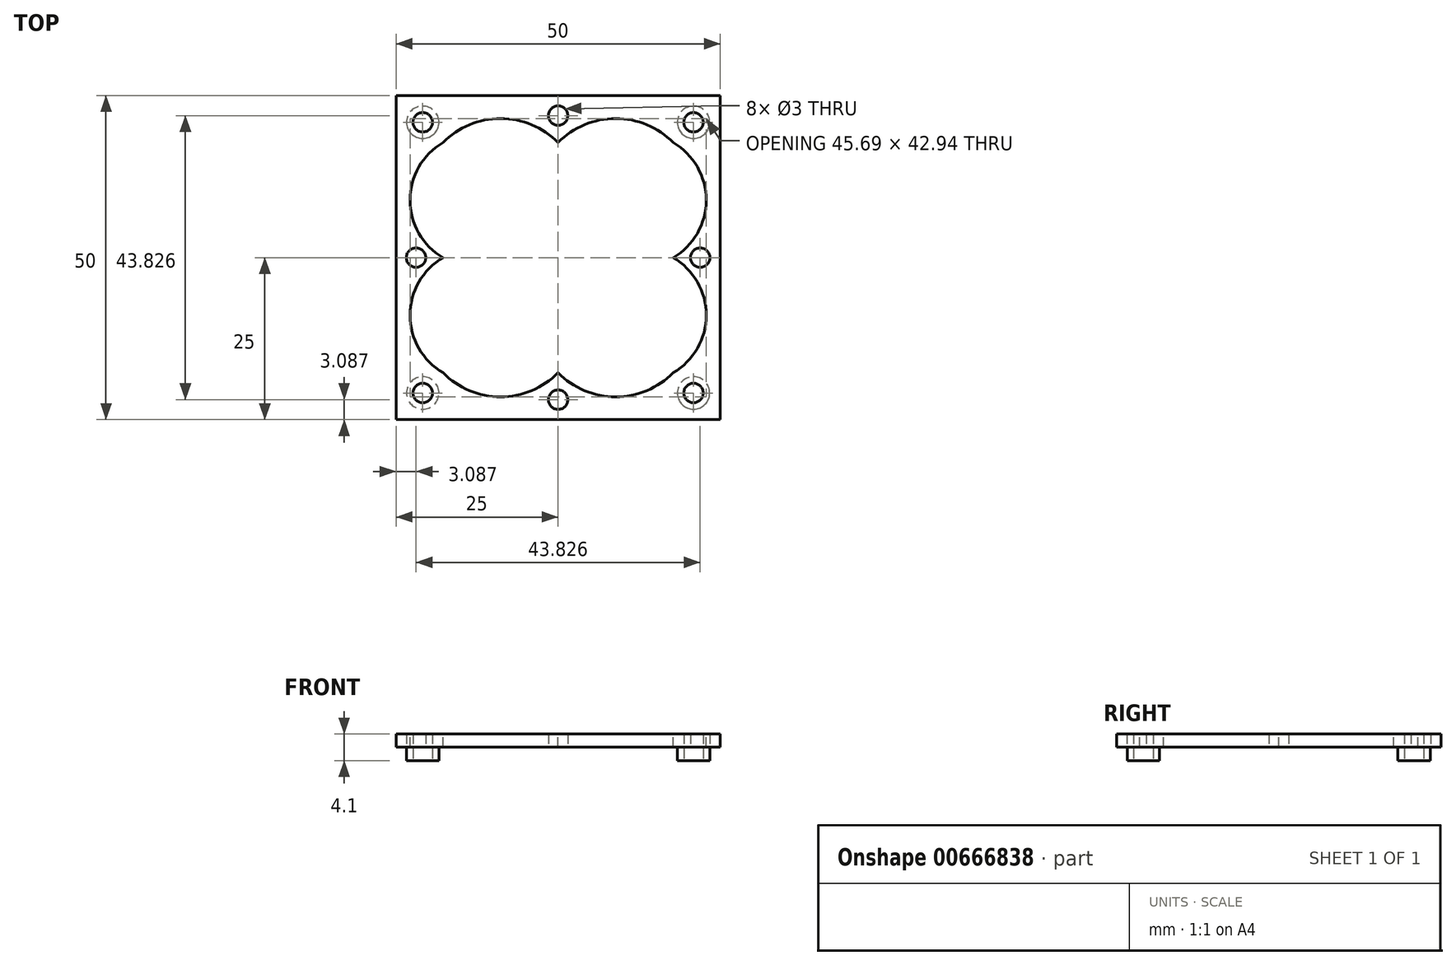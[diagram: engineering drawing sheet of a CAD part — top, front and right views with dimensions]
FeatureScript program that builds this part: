
annotation { "Feature Type Name" : "Feature", "Feature Type Description" : "" }
export const myFeature = defineFeature(function(context is Context, id is Id, definition is map)
    precondition{}
    {
        {
            var Q0;
            Q0=qCreatedBy(makeId("Top.planeOp"),FACE);
            var sketch = newSketch(context, id + "F0", { "sketchPlane" : qUnion([Q0])});
            skLineSegment(sketch, "E0.bottom", {"start": v(20.88, 20.89) * mm, "end": v(-20.89, 20.89) * mm, "construction": true});
            skLineSegment(sketch, "E0.top", {"start": v(20.89, -20.88) * mm, "end": v(-20.89, -20.89) * mm, "construction": true});
            skLineSegment(sketch, "E0.left", {"start": v(20.89, 20.89) * mm, "end": v(20.89, -20.88) * mm, "construction": true});
            skLineSegment(sketch, "E0.right", {"start": v(-20.89, 20.89) * mm, "end": v(-20.89, -20.89) * mm, "construction": true});
            skPoint(sketch, "E0.middle", {"position": v(0, 0) * mm});
            skCircle(sketch, "E1", {"center": v(-20.89, 20.89) * mm, "radius": 1.5 * mm});
            skCircle(sketch, "E2", {"center": v(20.88, 20.89) * mm, "radius": 1.5 * mm});
            skCircle(sketch, "E3", {"center": v(-20.89, -20.89) * mm, "radius": 1.5 * mm});
            skCircle(sketch, "E4", {"center": v(20.89, -20.88) * mm, "radius": 1.5 * mm});
            skCircle(sketch, "E5.cCircle", {"center": v(0, 0) * mm, "radius": 21.91 * mm, "construction": true});
            skLineSegment(sketch, "E5.0", {"start": v(21.91, 0) * mm, "end": v(0, -21.91) * mm, "construction": true});
            skLineSegment(sketch, "E5.1", {"start": v(0, -21.91) * mm, "end": v(-21.91, 0) * mm, "construction": true});
            skLineSegment(sketch, "E5.2", {"start": v(-21.91, 0) * mm, "end": v(0, 21.91) * mm, "construction": true});
            skLineSegment(sketch, "E5.3", {"start": v(0, 21.91) * mm, "end": v(21.91, 0) * mm, "construction": true});
            skLineSegment(sketch, "E6.bottom", {"start": v(25, 25) * mm, "end": v(-25, 25) * mm});
            skLineSegment(sketch, "E6.top", {"start": v(25, -25) * mm, "end": v(-25, -25) * mm});
            skLineSegment(sketch, "E6.left", {"start": v(25, 25) * mm, "end": v(25, -25) * mm});
            skLineSegment(sketch, "E6.right", {"start": v(-25, 25) * mm, "end": v(-25, -25) * mm});
            skCircle(sketch, "E7", {"center": v(0, 21.91) * mm, "radius": 1.5 * mm});
            skCircle(sketch, "E8", {"center": v(-21.91, 0) * mm, "radius": 1.5 * mm});
            skCircle(sketch, "E9", {"center": v(0, -21.91) * mm, "radius": 1.5 * mm});
            skCircle(sketch, "E10", {"center": v(21.91, 0) * mm, "radius": 1.5 * mm});
            skSolve(sketch);
        }
        {
            var Q0;
            Q0=makeQuery(id+"F0.imprint","IMPRINT",FACE,{"disambiguationData":[TD([[makeQuery(id+"F0.imprint","IMPRINT",EDGE,{"derivedFrom":sQuery(id+"F0.wireOp",EDGE,"E1")}),-1.0]])]});
            extrude(context, id + "F1", {"entities" : qUnion([Q0]), "depth" : 2 * mm, "offsetDistance" : 25 * mm});
        }
        {
            var Q0;
            Q0=makeQuery(id+"F1.opExtrude","CAP_FACE",FACE,{"disambiguationData":[OSD([sQuery(id+"F0.wireOp",EDGE,"E1"),sQuery(id+"F0.wireOp",EDGE,"E2"),sQuery(id+"F0.wireOp",EDGE,"E3"),sQuery(id+"F0.wireOp",EDGE,"E4"),sQuery(id+"F0.wireOp",EDGE,"E6.bottom"),sQuery(id+"F0.wireOp",EDGE,"E6.top"),sQuery(id+"F0.wireOp",EDGE,"E6.left"),sQuery(id+"F0.wireOp",EDGE,"E6.right"),sQuery(id+"F0.wireOp",EDGE,"E7"),sQuery(id+"F0.wireOp",EDGE,"E8"),sQuery(id+"F0.wireOp",EDGE,"E9"),sQuery(id+"F0.wireOp",EDGE,"E10")])],"isStart":false});
            var sketch = newSketch(context, id + "F2", { "sketchPlane" : qUnion([Q0])});
            skLineSegment(sketch, "E11.bottom", {"start": v(17.75, 17.75) * mm, "end": v(-17.75, 17.75) * mm, "construction": true});
            skLineSegment(sketch, "E11.top", {"start": v(17.75, -17.75) * mm, "end": v(-17.75, -17.75) * mm, "construction": true});
            skLineSegment(sketch, "E11.left", {"start": v(17.75, 17.75) * mm, "end": v(17.75, -17.75) * mm, "construction": true});
            skLineSegment(sketch, "E11.right", {"start": v(-17.75, 17.75) * mm, "end": v(-17.75, -17.75) * mm, "construction": true});
            skPoint(sketch, "E11.middle", {"position": v(0, 0) * mm});
            skArc(sketch, "E12", {"start": v(-17.75, 17.75) * mm, "mid": v(-22.84, 8.88) * mm, "end": v(-17.75, 0) * mm});
            skArc(sketch, "E13.MirrorCS", {"start": v(-17.75, -17.75) * mm, "mid": v(-22.84, -8.88) * mm, "end": v(-17.75, 0) * mm});
            skArc(sketch, "E14.MirrorCS", {"start": v(17.75, 17.75) * mm, "mid": v(22.84, 8.88) * mm, "end": v(17.75, 0) * mm});
            skArc(sketch, "E15.MirrorCS", {"start": v(17.75, -17.75) * mm, "mid": v(22.84, -8.88) * mm, "end": v(17.75, 0) * mm});
            skArc(sketch, "E16", {"start": v(0, 17.75) * mm, "mid": v(-8.88, 21.47) * mm, "end": v(-17.75, 17.75) * mm});
            skArc(sketch, "E17.MirrorCS", {"start": v(0, -17.75) * mm, "mid": v(-8.88, -21.47) * mm, "end": v(-17.75, -17.75) * mm});
            skArc(sketch, "E18.MirrorCS", {"start": v(0, 17.75) * mm, "mid": v(8.88, 21.47) * mm, "end": v(17.75, 17.75) * mm});
            skArc(sketch, "E19.MirrorCS", {"start": v(0, -17.75) * mm, "mid": v(8.88, -21.47) * mm, "end": v(17.75, -17.75) * mm});
            skSolve(sketch);
        }
        {
            var Q0;
            Q0=makeQuery(id+"F2.imprint","IMPRINT",FACE,{"disambiguationData":[TD([[makeQuery(id+"F2.imprint","IMPRINT",EDGE,{"derivedFrom":sQuery(id+"F2.wireOp",EDGE,"E12")}),1.0]])]});
            extrude(context, id + "F3", {"entities" : qUnion([Q0]), "operationType" : NewBodyOperationType.REMOVE, "oppositeDirection" : true, "depth" : 25 * mm, "offsetDistance" : 25 * mm});
        }
        {
            var Q0;
            Q0=makeQuery(id+"F1.opExtrude","CAP_FACE",FACE,{"disambiguationData":[OSD([sQuery(id+"F0.wireOp",EDGE,"E1"),sQuery(id+"F0.wireOp",EDGE,"E2"),sQuery(id+"F0.wireOp",EDGE,"E3"),sQuery(id+"F0.wireOp",EDGE,"E4"),sQuery(id+"F0.wireOp",EDGE,"E6.bottom"),sQuery(id+"F0.wireOp",EDGE,"E6.top"),sQuery(id+"F0.wireOp",EDGE,"E6.left"),sQuery(id+"F0.wireOp",EDGE,"E6.right"),sQuery(id+"F0.wireOp",EDGE,"E7"),sQuery(id+"F0.wireOp",EDGE,"E8"),sQuery(id+"F0.wireOp",EDGE,"E9"),sQuery(id+"F0.wireOp",EDGE,"E10")])],"isStart":true});
            var sketch = newSketch(context, id + "F4", { "sketchPlane" : qUnion([Q0])});
            skCircle(sketch, "E20", {"center": v(-20.89, 20.89) * mm, "radius": 2.5 * mm});
            skCircle(sketch, "E21", {"center": v(20.89, 20.88) * mm, "radius": 2.5 * mm});
            skCircle(sketch, "E22", {"center": v(20.88, -20.89) * mm, "radius": 2.5 * mm});
            skCircle(sketch, "E23", {"center": v(-20.89, -20.89) * mm, "radius": 2.5 * mm});
            skSolve(sketch);
        }
        {
            var Q0;
            Q0=makeQuery(id+"F4.imprint","IMPRINT",FACE,{"disambiguationData":[TD([[makeQuery(id+"F4.imprint","IMPRINT",EDGE,{"derivedFrom":sQuery(id+"F4.wireOp",EDGE,"E20")}),1.0]])]});
            var Q1;
            Q1=makeQuery(id+"F4.imprint","IMPRINT",FACE,{"disambiguationData":[TD([[makeQuery(id+"F4.imprint","IMPRINT",EDGE,{"derivedFrom":sQuery(id+"F4.wireOp",EDGE,"E21")}),1.0]])]});
            var Q2;
            Q2=makeQuery(id+"F4.imprint","IMPRINT",FACE,{"disambiguationData":[TD([[makeQuery(id+"F4.imprint","IMPRINT",EDGE,{"derivedFrom":sQuery(id+"F4.wireOp",EDGE,"E22")}),1.0]])]});
            var Q3;
            Q3=makeQuery(id+"F4.imprint","IMPRINT",FACE,{"disambiguationData":[TD([[makeQuery(id+"F4.imprint","IMPRINT",EDGE,{"derivedFrom":sQuery(id+"F4.wireOp",EDGE,"E23")}),1.0]])]});
            extrude(context, id + "F5", {"entities" : qUnion([Q0, Q1, Q2, Q3]), "operationType" : NewBodyOperationType.ADD, "depth" : 2.1 * mm, "offsetDistance" : 25 * mm});
        }
    });
